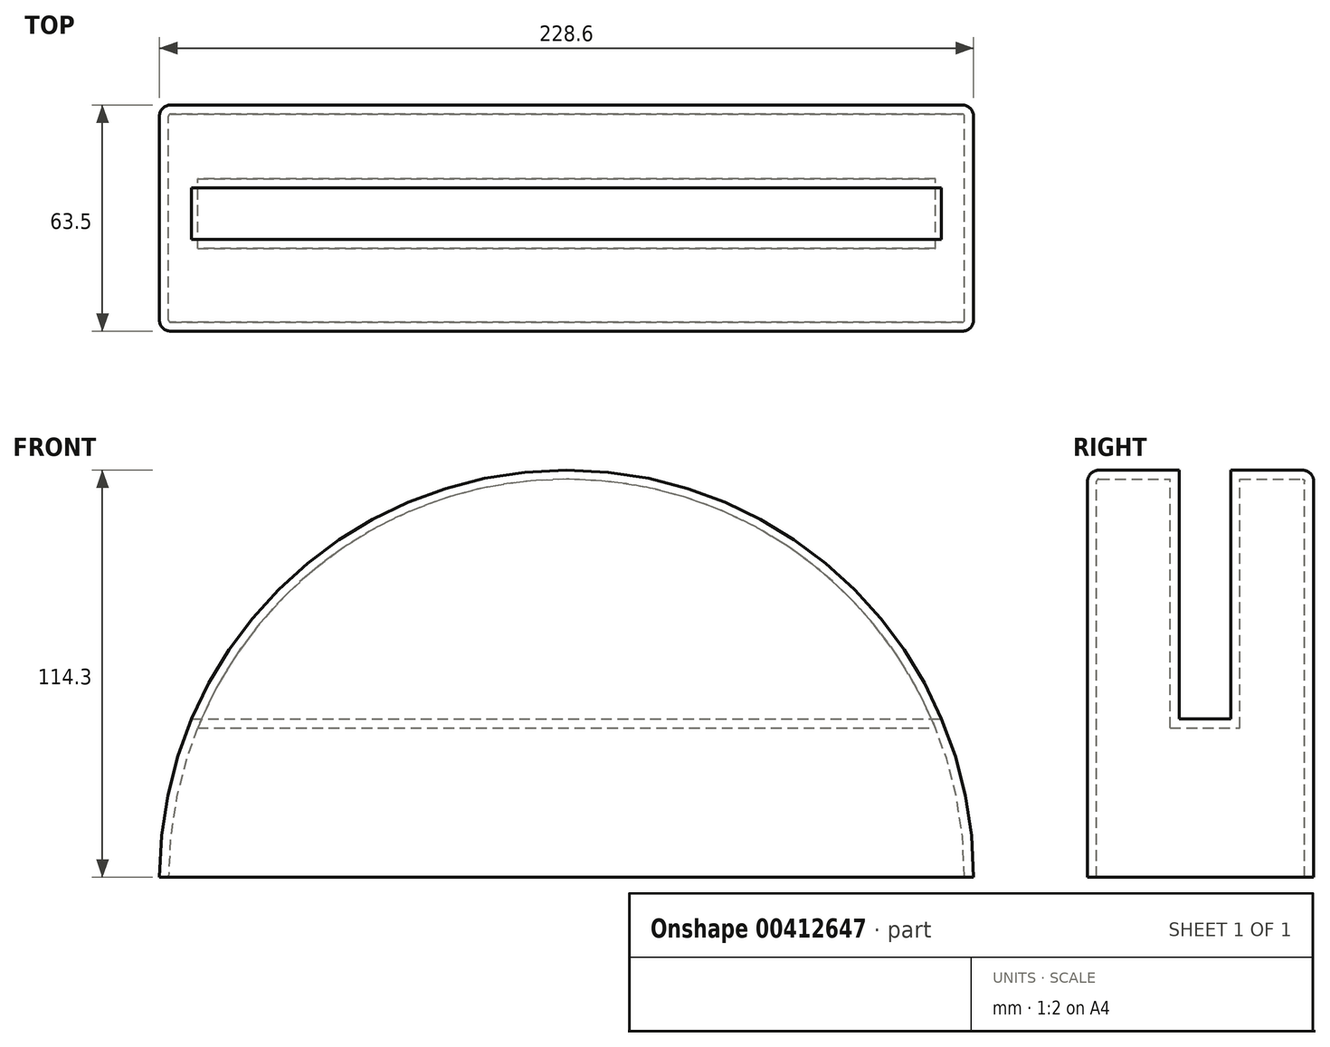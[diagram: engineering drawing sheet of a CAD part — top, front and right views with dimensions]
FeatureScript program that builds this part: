
annotation { "Feature Type Name" : "Feature", "Feature Type Description" : "" }
export const myFeature = defineFeature(function(context is Context, id is Id, definition is map)
    precondition{}
    {
        {
            var Q0;
            Q0=qCreatedBy(makeId("Front.planeOp"),FACE);
            var sketch = newSketch(context, id + "F0", { "sketchPlane" : qUnion([Q0])});
            skArc(sketch, "E0", {"start": v(114.3, 0) * mm, "mid": v(0, 114.3) * mm, "end": v(-114.3, 0) * mm});
            skLineSegment(sketch, "E1", {"start": v(-114.3, 0) * mm, "end": v(114.3, 0) * mm});
            skSolve(sketch);
        }
        {
            var Q0;
            Q0=makeQuery(id+"F0.imprint","IMPRINT",FACE,{"disambiguationData":[TD([[makeQuery(id+"F0.imprint","IMPRINT",EDGE,{"derivedFrom":sQuery(id+"F0.wireOp",EDGE,"E0")}),1.0]])]});
            extrude(context, id + "F1", {"entities" : qUnion([Q0]), "endBound" : BoundingType.SYMMETRIC, "depth" : 63.5 * mm});
        }
        {
            var Q0;
            Q0=qCreatedBy(makeId("Right.planeOp"),FACE);
            var sketch = newSketch(context, id + "F2", { "sketchPlane" : qUnion([Q0])});
            skLineSegment(sketch, "E2.bottom", {"start": v(8.53, 128.36) * mm, "end": v(-6.01, 128.36) * mm});
            skLineSegment(sketch, "E2.top", {"start": v(8.53, 44.51) * mm, "end": v(-6.01, 44.51) * mm});
            skLineSegment(sketch, "E2.left", {"start": v(8.53, 128.36) * mm, "end": v(8.53, 44.51) * mm});
            skLineSegment(sketch, "E2.right", {"start": v(-6.01, 128.36) * mm, "end": v(-6.01, 44.51) * mm});
            skSolve(sketch);
        }
        {
            var Q0;
            Q0 = qSketchRegion(id + "F2", true);
            extrude(context, id + "F3", {"entities" : qUnion([Q0]), "operationType" : NewBodyOperationType.REMOVE, "endBound" : BoundingType.THROUGH_ALL, "oppositeDirection" : true, "depth" : 25.4 * mm, "hasSecondDirection" : true, "secondDirectionBound" : SecondDirectionBoundingType.THROUGH_ALL, "secondDirectionOppositeDirection" : false, "secondDirectionDepth" : 25.4 * mm});
        }
        {
            var Q0;
            Q0=makeQuery(id+"F1.opExtrude","CAP_EDGE",EDGE,{"disambiguationData":[OSD([sQuery(id+"F0.wireOp",EDGE,"E0")])],"isStart":true});
            var Q1;
            Q1=makeQuery(id+"F1.opExtrude","CAP_EDGE",EDGE,{"disambiguationData":[OSD([sQuery(id+"F0.wireOp",EDGE,"E0")])],"isStart":false});
            fillet(context, id + "F4", {"entities" : qUnion([Q0, Q1]), "radius" : 3.17 * mm, "tangentPropagation" : true, "allowEdgeOverflow" : false});
        }
        {
            var Q0;
            Q0=makeQuery(id+"F1.opExtrude","SWEPT_FACE",FACE,{"disambiguationData":[OSD([sQuery(id+"F0.wireOp",EDGE,"E1")])]});
            shell(context, id + "F5", {"entities" : qUnion([Q0]), "thickness" : 2.54 * mm});
        }
        {
            var Q0;
            Q0=qCreatedBy(makeId("Top.planeOp"),FACE);
            cPlane(context, id + "F6", {"entities" : qUnion([Q0]), "cplaneType" : CPlaneType.OFFSET, "offset" : 152.4 * mm, "width" : 152.4 * mm, "height" : 152.4 * mm});
        }
    });
